# Revit family: 37_706000001_Grifería Lavamanos Sensor Electrónico
name_source: partatom
category: Aparatos sanitarios
revit_build: Autodesk Revit 2018 (Build: 20170223_1515(x64)
units: mm (PartAtom-declared; Revit-internal decimal feet)

## family parameters
Anfitrión = Cara
Compartido = No
Corte con vacíos al cargar = No
Cota de conector redondo = Diámetro de uso
Número OmniClass = 23.45.55.14
Punto de cálculo de habitación = No
Tipo de pieza = Normal
Título OmniClass = Single Faucets

## types (1)
- 37_706000001_Grifería Lavamanos Sensor Electrónico
    Accionamiento = Sin Contacto
    Caudal = 4.8 l/min (60 psi)
    Consumo de Agua = 4.8  l/min
    Cumple EDGE = NO
    Cumple LEED = NO
    Diametro conexión = 1/2 pulg. NPSM
    Elevación por defecto = 1219 mm
    Garantía = Garantía de 3 años por defectos de fabricación y cromados.
1 año de garantía para el sistema electrónico.
    Marca = CORONA
    Nombre = Grifería Lavamanos Sensor Electrónico
    Presión Máxima = 80 psi
    Presión Mínima = 10 psi
    Referencia = 706000001
    Tipo = Grifería Lavamanos
    Tráfico = Institucional Alto tráfico
    URL = https://www.corona.co
    Vida Util (ciclos) = 150000
